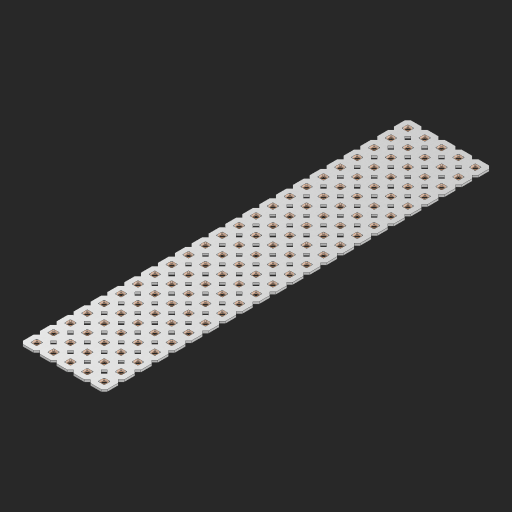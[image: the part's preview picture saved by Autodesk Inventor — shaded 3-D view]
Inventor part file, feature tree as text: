
AUTODESK INVENTOR PART (.ipt)
format: ipt  version: 2023 (Build 270158000, 158)  size: 1,614,336 bytes
history: native  units: in
note: dims shown in document units (in); Inventor stores cm internally (conversion verified against a paired STEP export)
features: other x116, extrude x114, sketch x2, pattern_linear x1
ambient origin geometry x8: Origin, YZ Plane, XZ Plane, XY Plane, X Axis, Y Axis, Z Axis, Center Point
bodies: Solid1 (feature_tree), Body (feature_tree)
feature tree (233):
  pattern_linear  "Rectangular Pattern1"  Spacing1=0.09in  [1 undecoded]
  sketch  "Sketch1"  dims[d1=0.5in]
  sketch  "Sketch2"  dims[d2=0.182in d3=0.09in d4=0.09in d5=0.09in d6=0.09in d7=0.09in d8=0.09in d9=0.09in d10=0.09in d11=0.02in d13=0.0in d14=0.172in d15=0.0625in d16=0.0in d19=0.5in d22=0.5in]
  other  "Srf1"
  other  "Srf126"
  other  "Srf127"
  other  "Srf128"
  other  "Srf129"
  other  "Srf130"
  other  "Srf131"
  other  "Srf250"
  other  "Srf251"
  other  "Srf252"
  other  "Srf253"
  other  "Srf254"
  other  "Srf255"
  other  "Srf256"
  other  "Srf257"
  other  "Srf258"
  other  "Srf259"
  other  "Srf260"
  other  "Srf261"
  other  "Srf262"
  other  "Srf263"
  other  "Srf264"
  other  "Srf265"
  other  "Srf268"
  other  "Srf269"
  other  "Srf270"
  other  "Srf271"
  other  "Srf272"
  other  "Srf273"
  other  "Srf274"
  other  "Srf275"
  other  "Srf276"
  other  "Srf277"
  other  "Srf278"
  other  "Srf279"
  other  "Srf280"
  other  "Srf281"
  other  "Srf282"
  other  "Srf283"
  other  "Srf284"
  other  "Srf285"
  other  "Srf286"
  other  "Srf287"
  other  "Srf288"
  other  "Srf289"
  other  "Srf290"
  other  "Srf293"
  other  "Srf294"
  other  "Srf295"
  other  "Srf296"
  other  "Srf297"
  other  "Srf298"
  other  "Srf299"
  other  "Srf300"
  other  "Srf301"
  other  "Srf302"
  other  "Srf303"
  other  "Srf304"
  other  "Srf305"
  other  "Srf306"
  other  "Srf307"
  other  "Srf308"
  other  "Srf309"
  other  "Srf310"
  other  "Srf311"
  other  "Srf312"
  other  "Srf313"
  other  "Srf314"
  other  "Srf315"
  other  "Srf318"
  other  "Srf319"
  other  "Srf320"
  other  "Srf321"
  other  "Srf322"
  other  "Srf323"
  other  "Srf324"
  other  "Srf325"
  other  "Srf326"
  other  "Srf327"
  other  "Srf328"
  other  "Srf329"
  other  "Srf330"
  other  "Srf331"
  other  "Srf332"
  other  "Srf333"
  other  "Srf334"
  other  "Srf335"
  other  "Srf336"
  other  "Srf337"
  other  "Srf338"
  other  "Srf339"
  other  "Srf340"
  other  "Srf343"
  other  "Srf344"
  other  "Srf345"
  other  "Srf346"
  other  "Srf347"
  other  "Srf348"
  other  "Srf349"
  other  "Srf350"
  other  "Srf351"
  other  "Srf352"
  other  "Srf353"
  other  "Srf354"
  other  "Srf355"
  other  "Srf356"
  other  "Srf357"
  other  "Srf358"
  other  "Srf359"
  other  "Srf360"
  other  "Srf361"
  other  "Srf362"
  other  "Srf363"
  other  "Srf364"
  other  "Srf365"
  other  "Circle"
  extrude  "ExtrusionSrf126"  Depth=0.09in
  extrude  "ExtrusionSrf127"  Depth=0.09in
  extrude  "ExtrusionSrf128"  Depth=0.09in
  extrude  "ExtrusionSrf129"  Depth=0.09in
  extrude  "ExtrusionSrf130"  Depth=0.09in
  extrude  "ExtrusionSrf131"  Depth=0.09in
  extrude  "ExtrusionSrf250"  Depth=0.09in
  extrude  "ExtrusionSrf251"  Depth=0.02in
  extrude  "ExtrusionSrf252"  TaperAngle=0.0deg  [1 undecoded]
  extrude  "ExtrusionSrf253"  Depth=0.5in
  extrude  "ExtrusionSrf254"  Depth=0.0625in TaperAngle=0.0deg
  extrude  "ExtrusionSrf255"  Depth=0.5in
  extrude  "ExtrusionSrf256"  Depth=0.5in
  extrude  "ExtrusionSrf257"  [1 undecoded]
  extrude  "ExtrusionSrf258"  [1 undecoded]
  extrude  "ExtrusionSrf259"  [1 undecoded]
  extrude  "ExtrusionSrf260"  [1 undecoded]
  extrude  "ExtrusionSrf261"  [1 undecoded]
  extrude  "ExtrusionSrf262"  [1 undecoded]
  extrude  "ExtrusionSrf263"  [1 undecoded]
  extrude  "ExtrusionSrf264"  [1 undecoded]
  extrude  "ExtrusionSrf265"  [1 undecoded]
  extrude  "ExtrusionSrf268"  [1 undecoded]
  extrude  "ExtrusionSrf269"  [1 undecoded]
  extrude  "ExtrusionSrf270"  [1 undecoded]
  extrude  "ExtrusionSrf271"  [1 undecoded]
  extrude  "ExtrusionSrf272"  [1 undecoded]
  extrude  "ExtrusionSrf273"  [1 undecoded]
  extrude  "ExtrusionSrf274"  [1 undecoded]
  extrude  "ExtrusionSrf275"  [1 undecoded]
  extrude  "ExtrusionSrf276"  [1 undecoded]
  extrude  "ExtrusionSrf277"  [1 undecoded]
  extrude  "ExtrusionSrf278"  [1 undecoded]
  extrude  "ExtrusionSrf279"  [1 undecoded]
  extrude  "ExtrusionSrf280"  [1 undecoded]
  extrude  "ExtrusionSrf281"  [1 undecoded]
  extrude  "ExtrusionSrf282"  [1 undecoded]
  extrude  "ExtrusionSrf283"  [1 undecoded]
  extrude  "ExtrusionSrf284"  [1 undecoded]
  extrude  "ExtrusionSrf285"  [1 undecoded]
  extrude  "ExtrusionSrf286"  [1 undecoded]
  extrude  "ExtrusionSrf287"  [1 undecoded]
  extrude  "ExtrusionSrf288"  [1 undecoded]
  extrude  "ExtrusionSrf289"  [1 undecoded]
  extrude  "ExtrusionSrf290"  [1 undecoded]
  extrude  "ExtrusionSrf293"  [1 undecoded]
  extrude  "ExtrusionSrf294"  [1 undecoded]
  extrude  "ExtrusionSrf295"  [1 undecoded]
  extrude  "ExtrusionSrf296"  [1 undecoded]
  extrude  "ExtrusionSrf297"  [1 undecoded]
  extrude  "ExtrusionSrf298"  [1 undecoded]
  extrude  "ExtrusionSrf299"  [1 undecoded]
  extrude  "ExtrusionSrf300"  [1 undecoded]
  extrude  "ExtrusionSrf301"  [1 undecoded]
  extrude  "ExtrusionSrf302"  [1 undecoded]
  extrude  "ExtrusionSrf303"  [1 undecoded]
  extrude  "ExtrusionSrf304"  [1 undecoded]
  extrude  "ExtrusionSrf305"  [1 undecoded]
  extrude  "ExtrusionSrf306"  [1 undecoded]
  extrude  "ExtrusionSrf307"  [1 undecoded]
  extrude  "ExtrusionSrf308"  [1 undecoded]
  extrude  "ExtrusionSrf309"  [1 undecoded]
  extrude  "ExtrusionSrf310"  [1 undecoded]
  extrude  "ExtrusionSrf311"  [1 undecoded]
  extrude  "ExtrusionSrf312"  [1 undecoded]
  extrude  "ExtrusionSrf313"  [1 undecoded]
  extrude  "ExtrusionSrf314"  [1 undecoded]
  extrude  "ExtrusionSrf315"  [1 undecoded]
  extrude  "ExtrusionSrf318"  [1 undecoded]
  extrude  "ExtrusionSrf319"  [1 undecoded]
  extrude  "ExtrusionSrf320"  [1 undecoded]
  extrude  "ExtrusionSrf321"  [1 undecoded]
  extrude  "ExtrusionSrf322"  [1 undecoded]
  extrude  "ExtrusionSrf323"  [1 undecoded]
  extrude  "ExtrusionSrf324"  [1 undecoded]
  extrude  "ExtrusionSrf325"  [1 undecoded]
  extrude  "ExtrusionSrf326"  [1 undecoded]
  extrude  "ExtrusionSrf327"  [1 undecoded]
  extrude  "ExtrusionSrf328"  [1 undecoded]
  extrude  "ExtrusionSrf329"  [1 undecoded]
  extrude  "ExtrusionSrf330"  [1 undecoded]
  extrude  "ExtrusionSrf331"  [1 undecoded]
  extrude  "ExtrusionSrf332"  [1 undecoded]
  extrude  "ExtrusionSrf333"  [1 undecoded]
  extrude  "ExtrusionSrf334"  [1 undecoded]
  extrude  "ExtrusionSrf335"  [1 undecoded]
  extrude  "ExtrusionSrf336"  [1 undecoded]
  extrude  "ExtrusionSrf337"  [1 undecoded]
  extrude  "ExtrusionSrf338"  [1 undecoded]
  extrude  "ExtrusionSrf339"  [1 undecoded]
  extrude  "ExtrusionSrf340"  [1 undecoded]
  extrude  "ExtrusionSrf343"  [1 undecoded]
  extrude  "ExtrusionSrf344"  [1 undecoded]
  extrude  "ExtrusionSrf345"  [1 undecoded]
  extrude  "ExtrusionSrf346"  [1 undecoded]
  extrude  "ExtrusionSrf347"  [1 undecoded]
  extrude  "ExtrusionSrf348"  [1 undecoded]
  extrude  "ExtrusionSrf349"  [1 undecoded]
  extrude  "ExtrusionSrf350"  [1 undecoded]
  extrude  "ExtrusionSrf351"  [1 undecoded]
  extrude  "ExtrusionSrf352"  [1 undecoded]
  extrude  "ExtrusionSrf353"  [1 undecoded]
  extrude  "ExtrusionSrf354"  [1 undecoded]
  extrude  "ExtrusionSrf355"  [1 undecoded]
  extrude  "ExtrusionSrf356"  [1 undecoded]
  extrude  "ExtrusionSrf357"  [1 undecoded]
  extrude  "ExtrusionSrf358"  [1 undecoded]
  extrude  "ExtrusionSrf359"  [1 undecoded]
  extrude  "ExtrusionSrf360"  [1 undecoded]
  extrude  "ExtrusionSrf361"  [1 undecoded]
  extrude  "ExtrusionSrf362"  [1 undecoded]
  extrude  "ExtrusionSrf363"  [1 undecoded]
  extrude  "ExtrusionSrf364"  [1 undecoded]
  extrude  "ExtrusionSrf365"  [1 undecoded]
note: 103 required parameter values undecoded (feature->parameter linkage not recoverable at this tier; creation-order binding heuristic only, values carry confidence <= 0.55)
